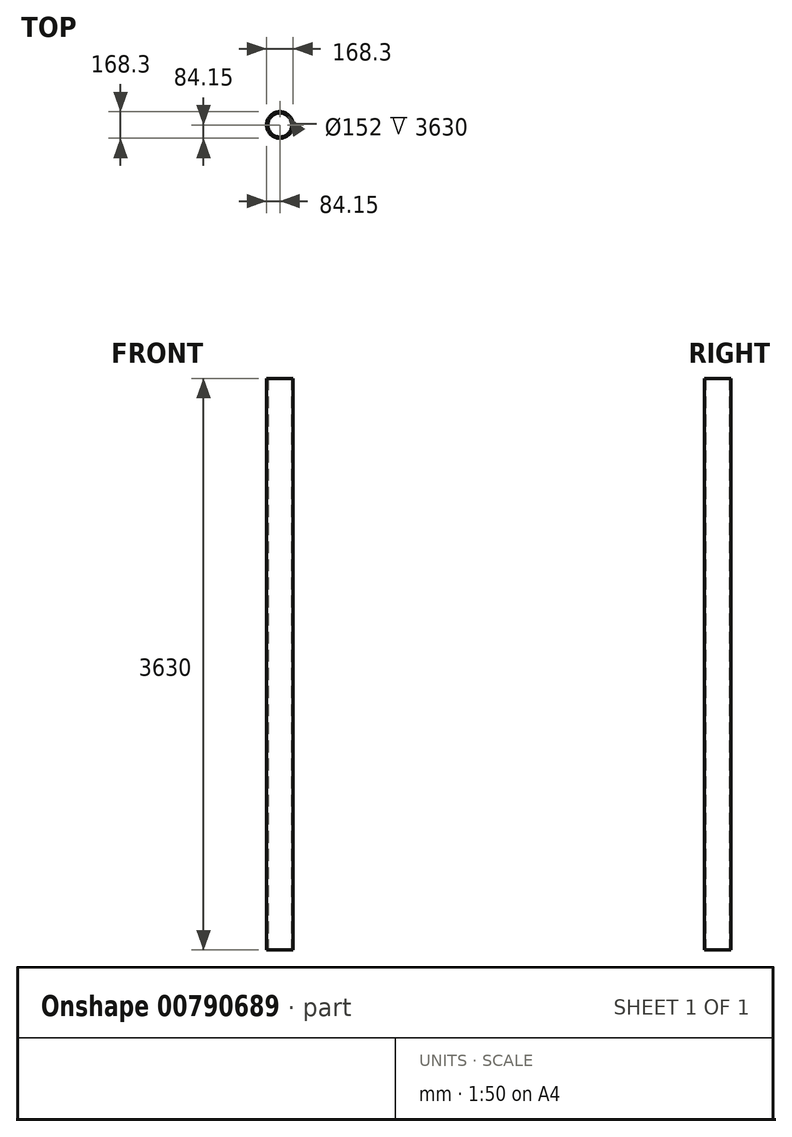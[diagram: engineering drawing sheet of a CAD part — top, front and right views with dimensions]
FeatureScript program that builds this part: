
annotation { "Feature Type Name" : "Feature", "Feature Type Description" : "" }
export const myFeature = defineFeature(function(context is Context, id is Id, definition is map)
    precondition{}
    {
        {
            var Q0;
            Q0=qCreatedBy(makeId("Top.planeOp"),FACE);
            var sketch = newSketch(context, id + "F0", { "sketchPlane" : qUnion([Q0])});
            skCircle(sketch, "E0", {"center": v(0, 0) * mm, "radius": 84.15 * mm});
            skCircle(sketch, "E1", {"center": v(0, 0) * mm, "radius": 76 * mm});
            skSolve(sketch);
        }
        {
            var Q0;
            Q0=makeQuery(id+"F0.imprint","IMPRINT",FACE,{"disambiguationData":[TD([[makeQuery(id+"F0.imprint","IMPRINT",EDGE,{"derivedFrom":sQuery(id+"F0.wireOp",EDGE,"E0")}),1.0]])]});
            extrude(context, id + "F1", {"entities" : qUnion([Q0]), "depth" : (3650 - 20) * mm, "offsetDistance" : 25 * mm});
        }
    });
